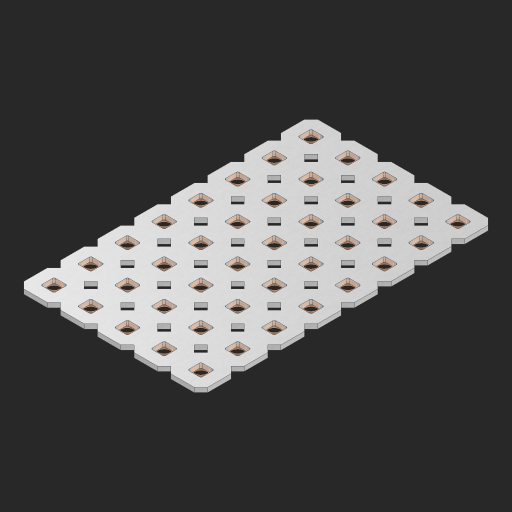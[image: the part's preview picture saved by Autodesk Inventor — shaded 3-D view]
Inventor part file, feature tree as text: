
AUTODESK INVENTOR PART (.ipt)
format: ipt  version: 2023 (Build 270158000, 158)  size: 762,368 bytes
history: native  units: in
note: dims shown in document units (in); Inventor stores cm internally (conversion verified against a paired STEP export)
features: other x41, extrude x39, sketch x2, pattern_linear x1
ambient origin geometry x8: Origin, YZ Plane, XZ Plane, XY Plane, X Axis, Y Axis, Z Axis, Center Point
bodies: Solid1 (feature_tree), Body (feature_tree)
feature tree (83):
  pattern_linear  "Rectangular Pattern1"  Spacing1=0.09in  [1 undecoded]
  sketch  "Sketch1"  dims[d1=0.5in]
  sketch  "Sketch2"  dims[d2=0.182in d3=0.09in d4=0.09in d5=0.09in d6=0.09in d7=0.09in d8=0.09in d9=0.09in d10=0.09in d11=0.02in d13=0.0in d14=0.172in d15=0.0625in d16=0.0in d19=0.5in d22=0.5in]
  other  "Srf1"
  other  "Srf126"
  other  "Srf127"
  other  "Srf128"
  other  "Srf129"
  other  "Srf130"
  other  "Srf131"
  other  "Srf250"
  other  "Srf268"
  other  "Srf269"
  other  "Srf270"
  other  "Srf271"
  other  "Srf272"
  other  "Srf273"
  other  "Srf274"
  other  "Srf275"
  other  "Srf293"
  other  "Srf294"
  other  "Srf295"
  other  "Srf296"
  other  "Srf297"
  other  "Srf298"
  other  "Srf299"
  other  "Srf300"
  other  "Srf318"
  other  "Srf319"
  other  "Srf320"
  other  "Srf321"
  other  "Srf322"
  other  "Srf323"
  other  "Srf324"
  other  "Srf325"
  other  "Srf343"
  other  "Srf344"
  other  "Srf345"
  other  "Srf346"
  other  "Srf347"
  other  "Srf348"
  other  "Srf349"
  other  "Srf350"
  other  "Circle"
  extrude  "ExtrusionSrf126"  Depth=0.09in
  extrude  "ExtrusionSrf127"  Depth=0.09in
  extrude  "ExtrusionSrf128"  Depth=0.09in
  extrude  "ExtrusionSrf129"  Depth=0.09in
  extrude  "ExtrusionSrf130"  Depth=0.09in
  extrude  "ExtrusionSrf131"  Depth=0.09in
  extrude  "ExtrusionSrf250"  Depth=0.09in
  extrude  "ExtrusionSrf268"  Depth=0.02in
  extrude  "ExtrusionSrf269"  TaperAngle=0.0deg  [1 undecoded]
  extrude  "ExtrusionSrf270"  Depth=0.5in
  extrude  "ExtrusionSrf271"  Depth=0.0625in TaperAngle=0.0deg
  extrude  "ExtrusionSrf272"  Depth=0.5in
  extrude  "ExtrusionSrf273"  Depth=0.5in
  extrude  "ExtrusionSrf274"  [1 undecoded]
  extrude  "ExtrusionSrf275"  [1 undecoded]
  extrude  "ExtrusionSrf293"  [1 undecoded]
  extrude  "ExtrusionSrf294"  [1 undecoded]
  extrude  "ExtrusionSrf295"  [1 undecoded]
  extrude  "ExtrusionSrf296"  [1 undecoded]
  extrude  "ExtrusionSrf297"  [1 undecoded]
  extrude  "ExtrusionSrf298"  [1 undecoded]
  extrude  "ExtrusionSrf299"  [1 undecoded]
  extrude  "ExtrusionSrf300"  [1 undecoded]
  extrude  "ExtrusionSrf318"  [1 undecoded]
  extrude  "ExtrusionSrf319"  [1 undecoded]
  extrude  "ExtrusionSrf320"  [1 undecoded]
  extrude  "ExtrusionSrf321"  [1 undecoded]
  extrude  "ExtrusionSrf322"  [1 undecoded]
  extrude  "ExtrusionSrf323"  [1 undecoded]
  extrude  "ExtrusionSrf324"  [1 undecoded]
  extrude  "ExtrusionSrf325"  [1 undecoded]
  extrude  "ExtrusionSrf343"  [1 undecoded]
  extrude  "ExtrusionSrf344"  [1 undecoded]
  extrude  "ExtrusionSrf345"  [1 undecoded]
  extrude  "ExtrusionSrf346"  [1 undecoded]
  extrude  "ExtrusionSrf347"  [1 undecoded]
  extrude  "ExtrusionSrf348"  [1 undecoded]
  extrude  "ExtrusionSrf349"  [1 undecoded]
  extrude  "ExtrusionSrf350"  [1 undecoded]
note: 28 required parameter values undecoded (feature->parameter linkage not recoverable at this tier; creation-order binding heuristic only, values carry confidence <= 0.55)
